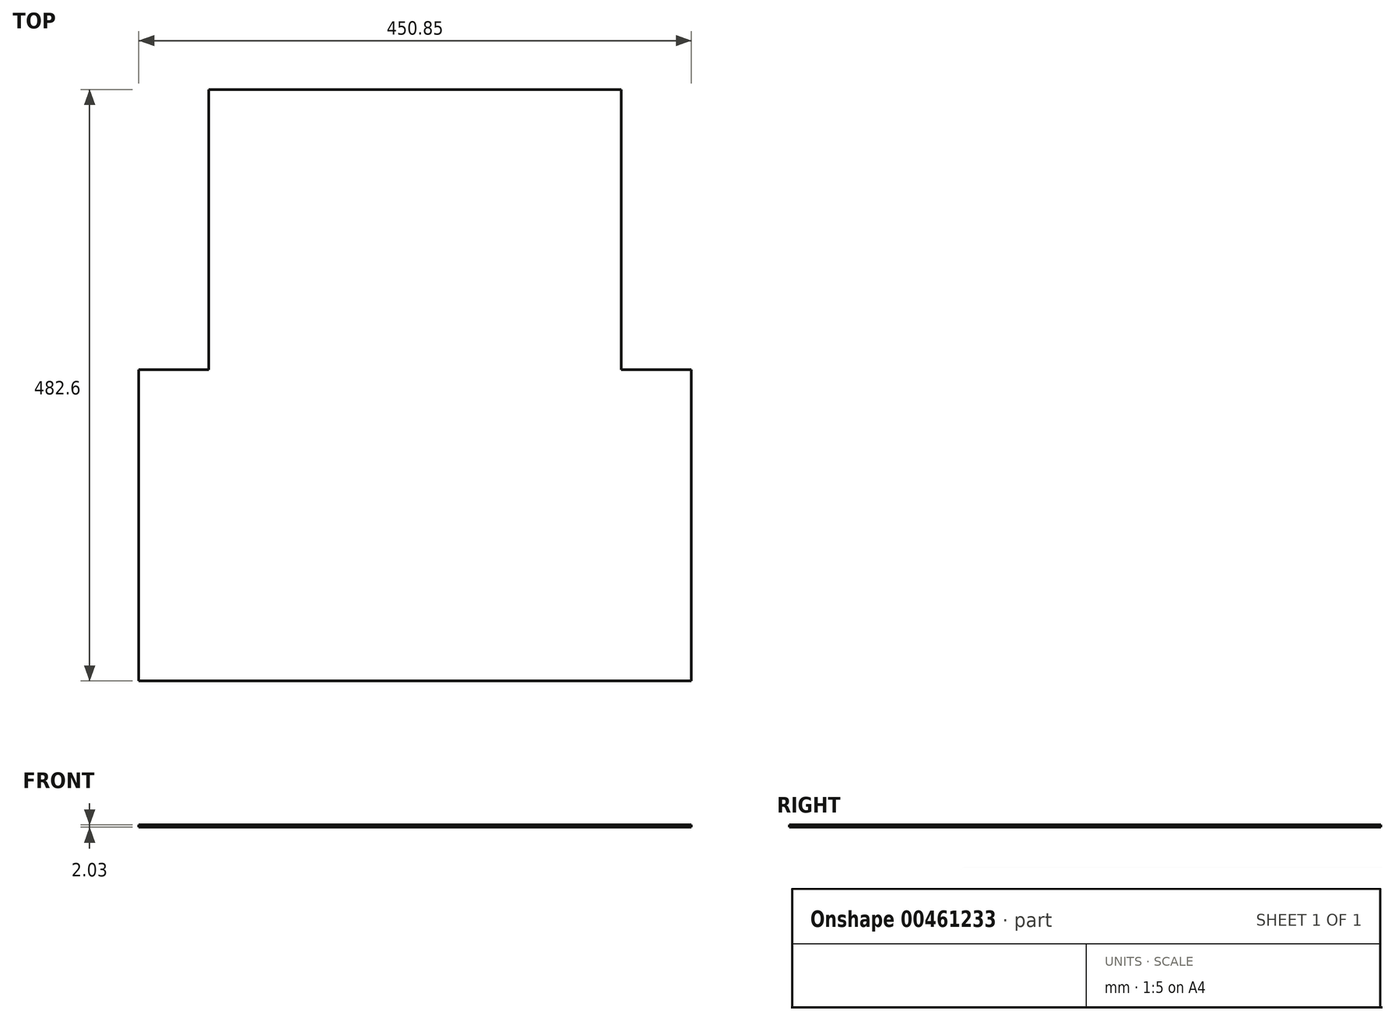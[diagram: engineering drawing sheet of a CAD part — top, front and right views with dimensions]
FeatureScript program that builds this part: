
annotation { "Feature Type Name" : "Feature", "Feature Type Description" : "" }
export const myFeature = defineFeature(function(context is Context, id is Id, definition is map)
    precondition{}
    {
        {
            var Q0;
            Q0=qCreatedBy(makeId("Top.planeOp"),FACE);
            var sketch = newSketch(context, id + "F0", { "sketchPlane" : qUnion([Q0])});
            skLineSegment(sketch, "E0", {"start": v(0, 254) * mm, "end": v(0, 0) * mm});
            skLineSegment(sketch, "E1", {"start": v(0, 0) * mm, "end": v(450.85, 0) * mm});
            skLineSegment(sketch, "E2", {"start": v(450.85, 0) * mm, "end": v(450.85, 254) * mm});
            skLineSegment(sketch, "E3", {"start": v(450.85, 254) * mm, "end": v(393.7, 254) * mm});
            skLineSegment(sketch, "E4", {"start": v(393.7, 254) * mm, "end": v(393.7, 482.6) * mm});
            skLineSegment(sketch, "E5", {"start": v(393.7, 482.6) * mm, "end": v(57.15, 482.6) * mm});
            skLineSegment(sketch, "E6", {"start": v(57.15, 482.6) * mm, "end": v(57.15, 254) * mm});
            skLineSegment(sketch, "E7", {"start": v(57.15, 254) * mm, "end": v(0, 254) * mm});
            skSolve(sketch);
        }
        {
            var Q0;
            Q0=makeQuery(id+"F0.imprint","IMPRINT",FACE,{"disambiguationData":[TD([[makeQuery(id+"F0.imprint","IMPRINT",EDGE,{"derivedFrom":sQuery(id+"F0.wireOp",EDGE,"E0")}),1.0]])]});
            extrude(context, id + "F1", {"entities" : qUnion([Q0]), "depth" : 2.03 * mm});
        }
    });
